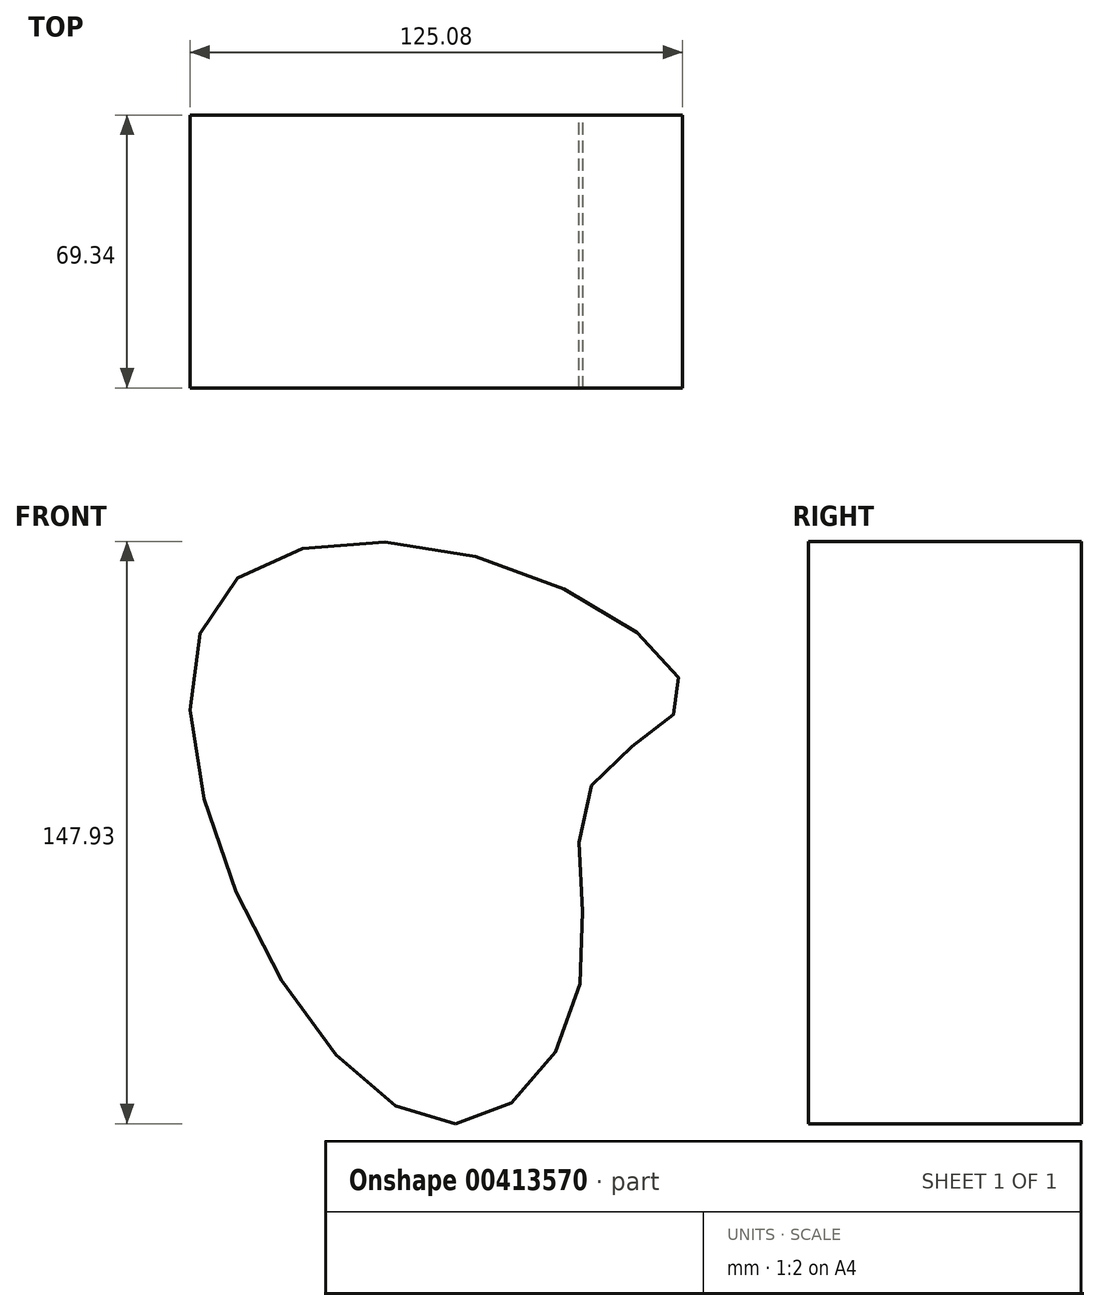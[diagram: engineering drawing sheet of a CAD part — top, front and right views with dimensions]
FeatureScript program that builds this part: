
annotation { "Feature Type Name" : "Feature", "Feature Type Description" : "" }
export const myFeature = defineFeature(function(context is Context, id is Id, definition is map)
    precondition{}
    {
        {
            var Q0;
            Q0=qCreatedBy(makeId("Front.planeOp"),FACE);
            var sketch = newSketch(context, id + "F0", { "sketchPlane" : qUnion([Q0])});
            skFitSpline(sketch, "E0", {"points": [v(0, -66.12) * mm, v(31.43, -31.73) * mm, v(34.99, 20.46) * mm, v(57.52, 41.8) * mm, v(11.27, 76.2) * mm, v(-59.9, 67.9) * mm, v(-52.78, -13.94) * mm, v(0, -66.12) * mm]});
            skSolve(sketch);
        }
        {
            var Q0;
            Q0=makeQuery(id+"F0.imprint","IMPRINT",FACE,{"disambiguationData":[TD([[makeQuery(id+"F0.imprint","IMPRINT",EDGE,{"derivedFrom":sQuery(id+"F0.wireOp",EDGE,"E0")}),1.0]])]});
            extrude(context, id + "F1", {"entities" : qUnion([Q0]), "depth" : 69.34 * mm, "offsetDistance" : 25.4 * mm});
        }
    });
